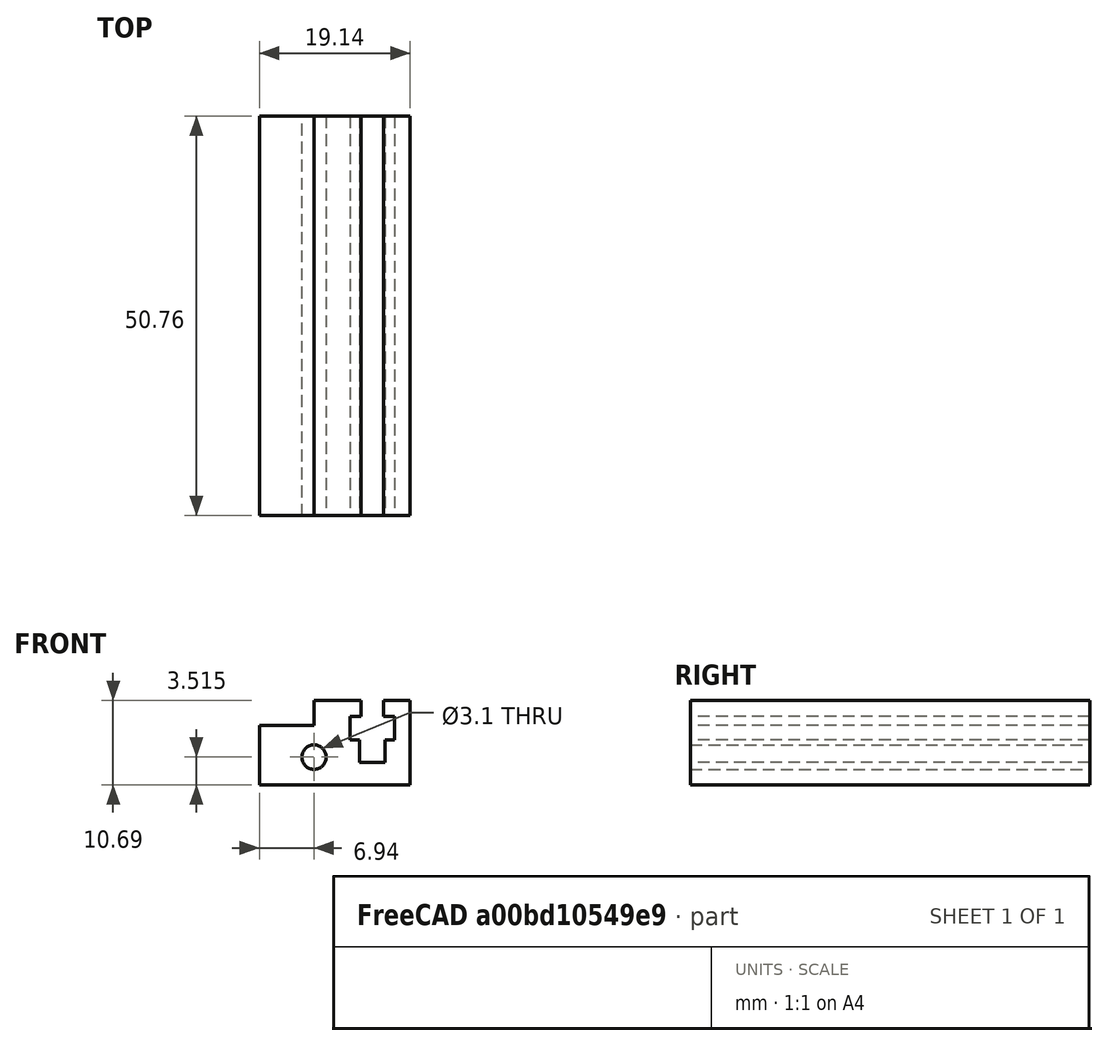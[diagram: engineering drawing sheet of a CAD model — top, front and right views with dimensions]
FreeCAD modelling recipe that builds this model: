
FCSTD DOCUMENT  (FreeCAD 0.20R29177 (Git))
Label: railholder
License: All rights reserved
LicenseURL: http://en.wikipedia.org/wiki/All_rights_reserved
objects: Sketcher::SketchObject×1, PartDesign::Pad×1, PartDesign::Body×1
note: 4 computed .brp shape members not serialized (recipe doc carries the construction recipe); baked Part::Feature solids carry a one-line shape summary decoded from their .brp

FEATURE [Sketcher::SketchObject] Sketch
  FullyConstrained = false
  MapMode = 5
  Placement = pos=(0,0,0) rot=(1,0,0;1.5708rad)
  Support = -> [XZ_Plane]
  sketch-geometry (27):
    g0: LineSegment StartX=-2.55 StartY=2.2 StartZ=0 EndX=2.55 EndY=2.2 EndZ=0
    g1: LineSegment StartX=2.55 StartY=2.2 StartZ=0 EndX=2.55 EndY=0 EndZ=0
    g2: LineSegment StartX=2.55 StartY=0 StartZ=0 EndX=-2.55 EndY=0 EndZ=0
    g3: LineSegment StartX=-2.55 StartY=0 StartZ=0 EndX=-2.55 EndY=2.2 EndZ=0
    g4: LineSegment StartX=-2.8 StartY=-0.419573 StartZ=0 EndX=-2.8 EndY=2.58043 EndZ=0
    g5: LineSegment StartX=-2.8 StartY=2.58043 StartZ=0 EndX=-1.4 EndY=2.58043 EndZ=0
    g6: LineSegment StartX=-1.4 StartY=2.58043 StartZ=0 EndX=-1.4 EndY=4.58043 EndZ=0
    g7: LineSegment StartX=-1.4 StartY=4.58043 StartZ=0 EndX=-7.4 EndY=4.58043 EndZ=0
    g8: LineSegment StartX=-7.4 StartY=4.58043 StartZ=0 EndX=-7.4 EndY=1.40543 EndZ=0
    g9: LineSegment StartX=-7.4 StartY=1.40543 StartZ=0 EndX=-14.3415 EndY=1.40543 EndZ=0
    g10: LineSegment StartX=-14.3415 StartY=1.40543 StartZ=0 EndX=-14.3415 EndY=-6.10986 EndZ=0
    g11: LineSegment StartX=-14.3415 StartY=-6.10986 StartZ=0 EndX=4.8 EndY=-6.10986 EndZ=0
    g12: LineSegment StartX=4.8 StartY=-6.10986 StartZ=0 EndX=4.8 EndY=4.58043 EndZ=0
    g13: LineSegment StartX=4.8 StartY=4.58043 StartZ=0 EndX=1.4 EndY=4.58043 EndZ=0
    g14: LineSegment StartX=1.4 StartY=4.58043 StartZ=0 EndX=1.4 EndY=2.58043 EndZ=0
    g15: LineSegment StartX=1.4 StartY=2.58043 StartZ=0 EndX=2.8 EndY=2.58043 EndZ=0
    g16: LineSegment StartX=2.8 StartY=2.58043 StartZ=0 EndX=2.8 EndY=-0.419573 EndZ=0
    g17: LineSegment StartX=2.8 StartY=-0.419573 StartZ=0 EndX=1.62351 EndY=-0.419573 EndZ=0
    g18: LineSegment StartX=-1.6 StartY=2.2 StartZ=0 EndX=1.6 EndY=2.2 EndZ=0
    g19: LineSegment StartX=1.6 StartY=2.2 StartZ=0 EndX=1.6 EndY=0 EndZ=0
    g20: LineSegment StartX=1.6 StartY=0 StartZ=0 EndX=-1.6 EndY=0 EndZ=0
    g21: LineSegment StartX=-1.6 StartY=0 StartZ=0 EndX=-1.6 EndY=2.2 EndZ=0
    g22: Circle CenterX=-7.4 CenterY=-2.59457 CenterZ=0 NormalX=0 NormalY=0 NormalZ=1 AngleXU=0 Radius=1.55
    g23: LineSegment StartX=-1.62351 StartY=-0.419573 StartZ=0 EndX=-1.62351 EndY=-3.25904 EndZ=0
    g24: LineSegment StartX=-1.62351 StartY=-3.25904 StartZ=0 EndX=1.62351 EndY=-3.25904 EndZ=0
    g25: LineSegment StartX=1.62351 StartY=-3.25904 StartZ=0 EndX=1.62351 EndY=-0.419573 EndZ=0
    g26: LineSegment StartX=-1.62351 StartY=-0.419573 StartZ=0 EndX=-2.8 EndY=-0.419573 EndZ=0
  constraints (72):
    c: Coincident(g0,g1)
    c: Coincident(g1,g2)
    c: Coincident(g2,g3)
    c: Coincident(g3,g0)
    c: Horizontal(g0)
    c: Horizontal(g2)
    c: Vertical(g1)
    c: Vertical(g3)
    c: DistanceX(g0,g0) = 5.1
    c: DistanceY(g3,g3) = 2.2
    c: Symmetric(g2,g1,g-1)
    c: Vertical(g4)
    c: Coincident(g4,g5)
    c: Horizontal(g5)
    c: Coincident(g5,g6)
    c: Vertical(g6)
    c: Coincident(g6,g7)
    c: Horizontal(g7)
    c: Coincident(g7,g8)
    c: Vertical(g8)
    c: Coincident(g8,g9)
    c: Horizontal(g9)
    c: Coincident(g9,g10)
    c: Vertical(g10)
    c: Coincident(g10,g11)
    c: Horizontal(g11)
    c: Coincident(g11,g12)
    c: Vertical(g12)
    c: Coincident(g12,g13)
    c: Horizontal(g13)
    c: Coincident(g13,g14)
    c: Vertical(g14)
    c: Coincident(g14,g15)
    c: Horizontal(g15)
    c: Coincident(g15,g16)
    c: Vertical(g16)
    c: Coincident(g16,g17)
    c: Coincident(g26,g4)
    c: Coincident(g18,g19)
    c: Coincident(g19,g20)
    c: Coincident(g20,g21)
    c: Coincident(g21,g18)
    c: Horizontal(g18)
    c: Horizontal(g20)
    c: Vertical(g19)
    c: Vertical(g21)
    c: PointOnObject(g18,g0)
    c: DistanceX(g18,g18) = 3.2
    c: Symmetric(g19,g20,g-1)
    c: DistanceY(g8,g8) = 3.175
    c: DistanceY(g6,g6) = 2
    c: Equal(g6,g14)
    c: Symmetric(g14,g5,g-2)
    c: DistanceX(g26,g17) = 5.6
    c: Symmetric(g4,g16,g-2)
    c: DistanceY(g4,g4) = 3
    c: Diameter(g22) = 3.1
    c: DistanceX(g15,g12) = 2
    c: Vertical(g8,g22)
    c: DistanceX(g7,g7) = 6
    c: DistanceX(g7,g-1) = 7.4
    c: DistanceX(g15,g15) = 1.4
    c: Vertical(g23)
    c: Coincident(g23,g24)
    c: Coincident(g24,g25)
    c: Vertical(g25)
    c: Symmetric(g24,g23,g-2)
    c: Coincident(g17,g25)
    c: Coincident(g26,g23)
    c: DistanceY(g22,g8) = 4
    c: Horizontal(g17)
    c: Horizontal(g26)
FEATURE [PartDesign::Pad] Pad
  Direction = (0,-1,-2e-16)
  Length = 50.75
  Length2 = 10
  Midplane = true
  Placement = pos=(0,0,0) rot=(1,0,0;1.5708rad)
  Profile = -> Sketch
  ReferenceAxis = -> Sketch [N_Axis]
  Type = 0
FEATURE [PartDesign::Body] Body
  Group = -> [Sketch,Pad]
  Origin = -> Origin
  Tip = -> Pad
